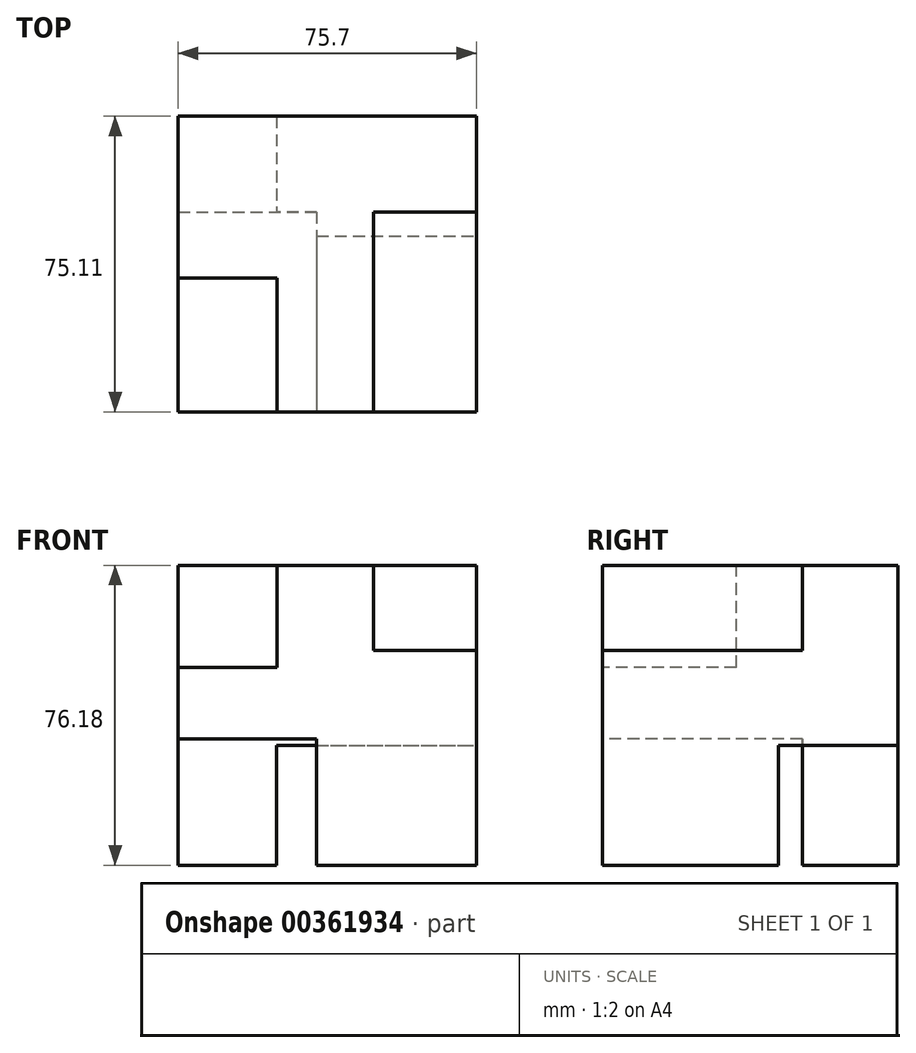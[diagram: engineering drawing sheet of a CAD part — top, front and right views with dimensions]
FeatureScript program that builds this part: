
annotation { "Feature Type Name" : "Feature", "Feature Type Description" : "" }
export const myFeature = defineFeature(function(context is Context, id is Id, definition is map)
    precondition{}
    {
        {
            var Q0;
            Q0=qCreatedBy(makeId("Top.planeOp"),FACE);
            var sketch = newSketch(context, id + "F0", { "sketchPlane" : qUnion([Q0])});
            skLineSegment(sketch, "E0.bottom", {"start": v(0, 0) * mm, "end": v(75.7, 0) * mm});
            skLineSegment(sketch, "E0.top", {"start": v(0, -75.1) * mm, "end": v(75.7, -75.1) * mm});
            skLineSegment(sketch, "E0.left", {"start": v(0, 0) * mm, "end": v(0, -75.1) * mm});
            skLineSegment(sketch, "E0.right", {"start": v(75.7, 0) * mm, "end": v(75.7, -75.1) * mm});
            skSolve(sketch);
        }
        {
            var Q0;
            Q0=makeQuery(id+"F0.imprint","IMPRINT",FACE,{"disambiguationData":[TD([[makeQuery(id+"F0.imprint","IMPRINT",EDGE,{"derivedFrom":sQuery(id+"F0.wireOp",EDGE,"E0.bottom")}),-1.0]])]});
            extrude(context, id + "F1", {"entities" : qUnion([Q0]), "depth" : 76.18 * mm});
        }
        {
            var Q0;
            Q0=makeQuery(id+"F1.opExtrude","SWEPT_FACE",FACE,{"disambiguationData":[OSD([sQuery(id+"F0.wireOp",EDGE,"E0.top")])]});
            var sketch = newSketch(context, id + "F2", { "sketchPlane" : qUnion([Q0])});
            skLineSegment(sketch, "E1", {"start": v(0, 76.18) * mm, "end": v(37.85, 40.04) * mm});
            skPoint(sketch, "E1.endSnap0", {"position": v(37.85, 76.18) * mm});
            skLineSegment(sketch, "E2", {"start": v(37.85, 40.04) * mm, "end": v(75.7, 76.18) * mm});
            skLineSegment(sketch, "E3", {"start": v(75.7, 76.18) * mm, "end": v(0, 0) * mm});
            skLineSegment(sketch, "E4", {"start": v(0, 0) * mm, "end": v(75.7, 0) * mm});
            skLineSegment(sketch, "E5", {"start": v(75.7, 0) * mm, "end": v(37.85, 40.04) * mm});
            skSolve(sketch);
        }
        {
            var Q0;
            Q0 = qSketchRegion(id + "F2", true);
            var Q1;
            Q1=makeQuery(id+"F2.imprint","IMPRINT",FACE,{"disambiguationData":[TD([[makeQuery(id+"F2.imprint","IMPRINT",EDGE,{"derivedFrom":sQuery(id+"F2.wireOp",EDGE,"E1")}),1.0]])]});
            extrude(context, id + "F3", {"entities" : qUnion([Q0, Q1]), "operationType" : NewBodyOperationType.ADD, "oppositeDirection" : true, "depth" : 7.56 * mm});
        }
        {
            var Q0;
            Q0=makeQuery(id+"F1.opExtrude","SWEPT_FACE",FACE,{"disambiguationData":[OSD([sQuery(id+"F0.wireOp",EDGE,"E0.top")])]});
            var sketch = newSketch(context, id + "F4", { "sketchPlane" : qUnion([Q0])});
            skSolve(sketch);
        }
        {
            var Q0;
            {var subQ0=sQuery(id+"F0.wireOp",EDGE,"E0.top");Q0=makeQuery(id+"F4.imprint","IMPRINT",FACE,{"disambiguationData":[TD([[makeQuery(id+"F4.imprint","IMPRINT",EDGE,{"derivedFrom":makeQuery(id+"F1.opExtrude","CAP_EDGE",EDGE,{"disambiguationData":[OSD([subQ0])],"isStart":true})}),1.0]])]});}
            extrude(context, id + "F5", {"entities" : qUnion([Q0]), "operationType" : NewBodyOperationType.ADD, "oppositeDirection" : true, "depth" : 70.37 * mm});
        }
        {
            var Q0;
            Q0=makeQuery(id+"F1.opExtrude","SWEPT_FACE",FACE,{"disambiguationData":[OSD([sQuery(id+"F0.wireOp",EDGE,"E0.top")])]});
            var sketch = newSketch(context, id + "F6", { "sketchPlane" : qUnion([Q0])});
            skLineSegment(sketch, "E6.bottom", {"start": v(0, 0) * mm, "end": v(35.17, 0) * mm});
            skLineSegment(sketch, "E6.top", {"start": v(0, 32.14) * mm, "end": v(35.17, 32.14) * mm});
            skLineSegment(sketch, "E6.left", {"start": v(0, 0) * mm, "end": v(0, 32.14) * mm});
            skLineSegment(sketch, "E6.right", {"start": v(35.17, 0) * mm, "end": v(35.17, 32.14) * mm});
            skSolve(sketch);
        }
        {
            var Q0;
            Q0=makeQuery(id+"F6.imprint","IMPRINT",FACE,{"disambiguationData":[TD([[makeQuery(id+"F6.imprint","IMPRINT",EDGE,{"derivedFrom":sQuery(id+"F6.wireOp",EDGE,"E6.bottom")}),1.0]])]});
            extrude(context, id + "F7", {"entities" : qUnion([Q0]), "operationType" : NewBodyOperationType.REMOVE, "oppositeDirection" : true, "depth" : 50.8 * mm});
        }
        {
            var Q0;
            Q0=makeQuery(id+"F1.opExtrude","SWEPT_FACE",FACE,{"disambiguationData":[OSD([sQuery(id+"F0.wireOp",EDGE,"E0.top")])]});
            var sketch = newSketch(context, id + "F8", { "sketchPlane" : qUnion([Q0])});
            skLineSegment(sketch, "E7.bottom", {"start": v(75.7, 76.18) * mm, "end": v(49.56, 76.18) * mm});
            skLineSegment(sketch, "E7.top", {"start": v(75.7, 54.61) * mm, "end": v(49.56, 54.61) * mm});
            skLineSegment(sketch, "E7.left", {"start": v(75.7, 76.18) * mm, "end": v(75.7, 54.61) * mm});
            skLineSegment(sketch, "E7.right", {"start": v(49.56, 76.18) * mm, "end": v(49.56, 54.61) * mm});
            skSolve(sketch);
        }
        {
            var Q0;
            Q0=makeQuery(id+"F8.imprint","IMPRINT",FACE,{"disambiguationData":[TD([[makeQuery(id+"F8.imprint","IMPRINT",EDGE,{"derivedFrom":sQuery(id+"F8.wireOp",EDGE,"E7.bottom")}),-1.0]])]});
            extrude(context, id + "F9", {"entities" : qUnion([Q0]), "operationType" : NewBodyOperationType.REMOVE, "oppositeDirection" : true, "depth" : 50.8 * mm});
        }
        {
            var Q0;
            Q0=makeQuery(id+"F1.opExtrude","SWEPT_FACE",FACE,{"disambiguationData":[OSD([sQuery(id+"F0.wireOp",EDGE,"E0.right")])]});
            var sketch = newSketch(context, id + "F10", { "sketchPlane" : qUnion([Q0])});
            skLineSegment(sketch, "E8.bottom", {"start": v(0, 0) * mm, "end": v(-30.39, 0) * mm});
            skLineSegment(sketch, "E8.top", {"start": v(0, 30.48) * mm, "end": v(-30.39, 30.48) * mm});
            skLineSegment(sketch, "E8.left", {"start": v(0, 0) * mm, "end": v(0, 30.48) * mm});
            skLineSegment(sketch, "E8.right", {"start": v(-30.39, 0) * mm, "end": v(-30.39, 30.48) * mm});
            skSolve(sketch);
        }
        {
            var Q0;
            Q0=makeQuery(id+"F10.imprint","IMPRINT",FACE,{"disambiguationData":[TD([[makeQuery(id+"F10.imprint","IMPRINT",EDGE,{"derivedFrom":sQuery(id+"F10.wireOp",EDGE,"E8.bottom")}),-1.0]])]});
            extrude(context, id + "F11", {"entities" : qUnion([Q0]), "operationType" : NewBodyOperationType.REMOVE, "oppositeDirection" : true, "depth" : 50.8 * mm});
        }
        {
            var Q0;
            Q0=makeQuery(id+"F1.opExtrude","CAP_FACE",FACE,{"disambiguationData":[OSD([sQuery(id+"F0.wireOp",EDGE,"E0.bottom"),sQuery(id+"F0.wireOp",EDGE,"E0.top"),sQuery(id+"F0.wireOp",EDGE,"E0.left"),sQuery(id+"F0.wireOp",EDGE,"E0.right")])],"isStart":false});
            var sketch = newSketch(context, id + "F12", { "sketchPlane" : qUnion([Q0])});
            skLineSegment(sketch, "E9.bottom", {"start": v(0, -75.1) * mm, "end": v(25.12, -75.1) * mm});
            skLineSegment(sketch, "E9.top", {"start": v(0, -41.05) * mm, "end": v(25.12, -41.05) * mm});
            skLineSegment(sketch, "E9.left", {"start": v(0, -75.1) * mm, "end": v(0, -41.05) * mm});
            skLineSegment(sketch, "E9.right", {"start": v(25.12, -75.1) * mm, "end": v(25.12, -41.05) * mm});
            skSolve(sketch);
        }
        {
            var Q0;
            Q0 = qSketchRegion(id + "F12", true);
            var sketch = newSketch(context, id + "F13", { "sketchPlane" : qUnion([Q0])});
            skSolve(sketch);
        }
        {
            var Q0;
            Q0=makeQuery(id+"F13.imprint","IMPRINT",FACE,{"disambiguationData":[TD([[makeQuery(id+"F13.imprint","IMPRINT",EDGE,{"derivedFrom":makeQuery(id+"F12.imprint","IMPRINT",EDGE,{"derivedFrom":sQuery(id+"F12.wireOp",EDGE,"E9.bottom")})}),1.0]])]});
            extrude(context, id + "F14", {"entities" : qUnion([Q0]), "operationType" : NewBodyOperationType.REMOVE, "oppositeDirection" : true, "depth" : 25.87 * mm});
        }
    });
